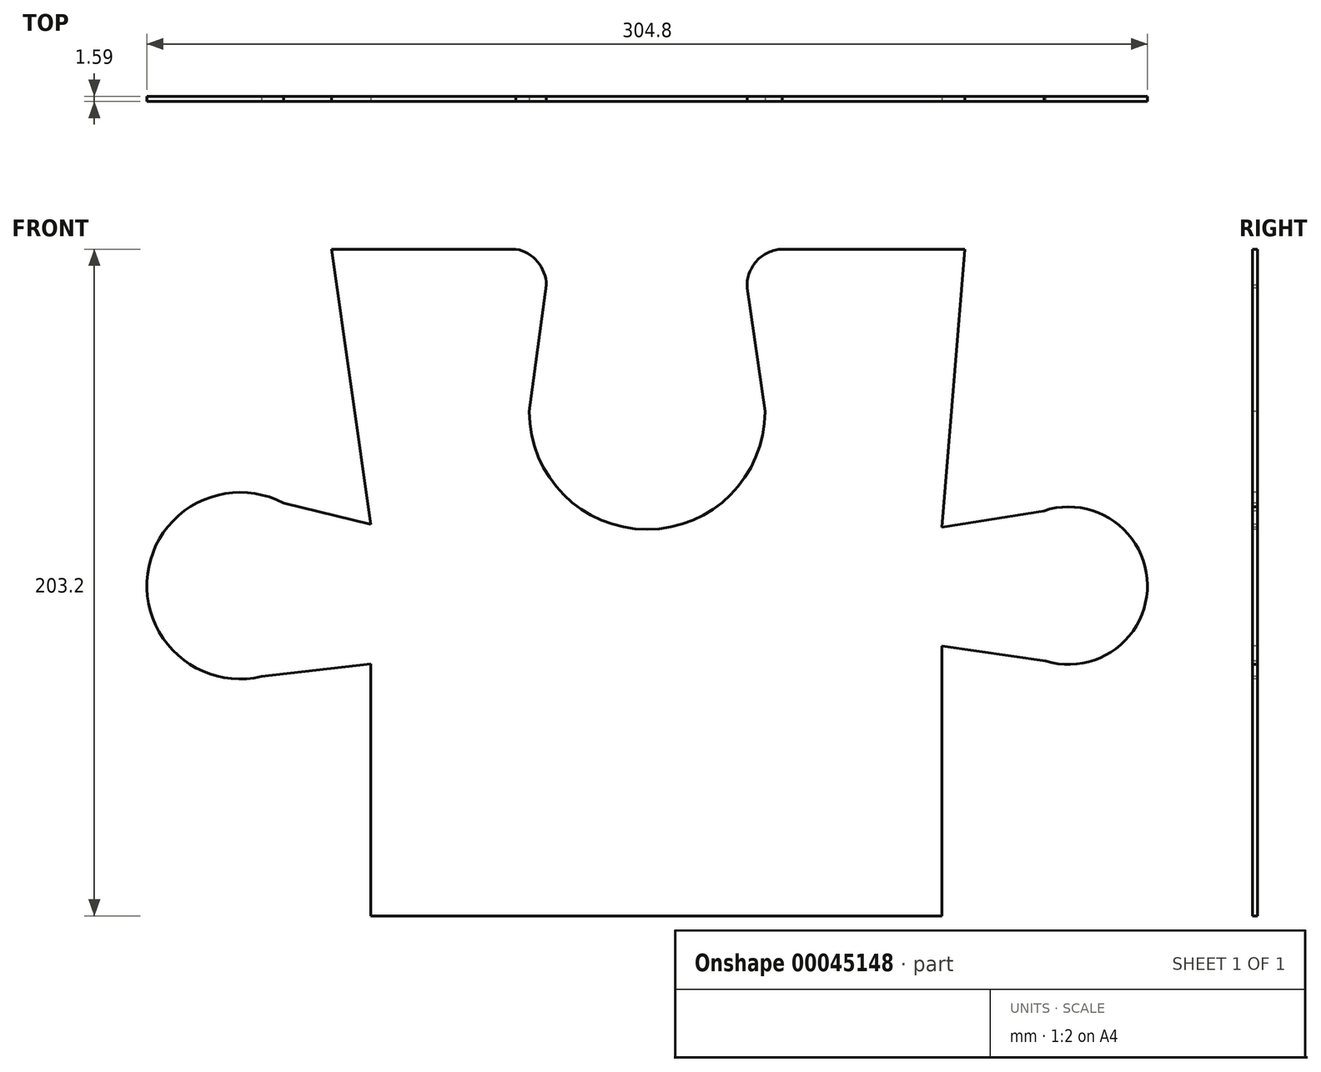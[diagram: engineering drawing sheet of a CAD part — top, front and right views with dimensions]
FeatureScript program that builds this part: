
annotation { "Feature Type Name" : "Feature", "Feature Type Description" : "" }
export const myFeature = defineFeature(function(context is Context, id is Id, definition is map)
    precondition{}
    {
        {
            var Q0;
            Q0=qCreatedBy(makeId("Front.planeOp"),FACE);
            var sketch = newSketch(context, id + "F0", { "sketchPlane" : qUnion([Q0])});
            skLineSegment(sketch, "E0.bottom", {"start": v(-101.92, -100.63) * mm, "end": v(202.88, -100.63) * mm});
            skLineSegment(sketch, "E0.top", {"start": v(-101.92, 102.57) * mm, "end": v(202.88, 102.57) * mm});
            skLineSegment(sketch, "E0.left", {"start": v(-101.92, -100.63) * mm, "end": v(-101.92, 102.57) * mm});
            skLineSegment(sketch, "E0.right", {"start": v(202.88, -100.63) * mm, "end": v(202.88, 102.57) * mm});
            skSolve(sketch);
        }
        {
            var Q0;
            Q0=makeQuery(id+"F0.imprint","IMPRINT",FACE,{"disambiguationData":[TD([[makeQuery(id+"F0.imprint","IMPRINT",EDGE,{"derivedFrom":sQuery(id+"F0.wireOp",EDGE,"E0.bottom")}),1.0]])]});
            extrude(context, id + "F1", {"entities" : qUnion([Q0]), "depth" : 1.59 * mm});
        }
        {
            var Q0;
            Q0=makeQuery(id+"F1.opExtrude","CAP_FACE",FACE,{"disambiguationData":[OSD([sQuery(id+"F0.wireOp",EDGE,"E0.bottom"),sQuery(id+"F0.wireOp",EDGE,"E0.top"),sQuery(id+"F0.wireOp",EDGE,"E0.left"),sQuery(id+"F0.wireOp",EDGE,"E0.right")])],"isStart":false});
            var sketch = newSketch(context, id + "F2", { "sketchPlane" : qUnion([Q0])});
            skCircle(sketch, "E1", {"center": v(50.48, 53.07) * mm, "radius": 35.9 * mm});
            skPoint(sketch, "E1.centerSnap0", {"position": v(50.48, 102.57) * mm});
            skLineSegment(sketch, "E2", {"start": v(14.58, 53.07) * mm, "end": v(21.26, 102.57) * mm});
            skLineSegment(sketch, "E3", {"start": v(21.26, 102.57) * mm, "end": v(79.23, 102.57) * mm});
            skLineSegment(sketch, "E4", {"start": v(79.23, 102.57) * mm, "end": v(86.38, 53.07) * mm});
            skSolve(sketch);
        }
        {
            var Q0;
            {var subQ1=sQuery(id+"F2.wireOp",EDGE,"E1");var subQ4=sQuery(id+"F2.wireOp",EDGE,"E4");var subQ5=makeQuery(id+"F2.imprint","INTERSECT",VERTEX,{"disambiguationData":[OD(1.0)],"derivedFrom":[subQ1,subQ4]});Q0=makeQuery(id+"F2.imprint","IMPRINT",FACE,{"disambiguationData":[TD([[makeQuery(id+"F2.imprint","IMPRINT",EDGE,{"disambiguationData":[TD([[subQ5,-1.0]])],"derivedFrom":subQ1}),1.0]])]});}
            var Q1;
            {var subQ4=sQuery(id+"F2.wireOp",EDGE,"E3");Q1=makeQuery(id+"F2.imprint","IMPRINT",FACE,{"disambiguationData":[TD([[makeQuery(id+"F2.imprint","IMPRINT",EDGE,{"derivedFrom":subQ4}),-1.0]])]});}
            extrude(context, id + "F3", {"entities" : qUnion([Q0, Q1]), "operationType" : NewBodyOperationType.REMOVE, "oppositeDirection" : true, "depth" : 50.8 * mm});
        }
        {
            var Q0;
            Q0=makeQuery(id+"F1.opExtrude","CAP_FACE",FACE,{"disambiguationData":[OSD([sQuery(id+"F0.wireOp",EDGE,"E0.bottom"),sQuery(id+"F0.wireOp",EDGE,"E0.top"),sQuery(id+"F0.wireOp",EDGE,"E0.left"),sQuery(id+"F0.wireOp",EDGE,"E0.right")])],"isStart":false});
            var sketch = newSketch(context, id + "F4", { "sketchPlane" : qUnion([Q0])});
            skArc(sketch, "E5", {"start": v(19.78, 91.61) * mm, "mid": v(15.62, 100.21) * mm, "end": v(6.36, 102.57) * mm});
            skSolve(sketch);
        }
        {
            var Q0;
            {var subQ1=sQuery(id+"F2.wireOp",EDGE,"E2");var subQ4=sQuery(id+"F4.wireOp",EDGE,"E5");var subQ6=makeQuery(id+"F3.boolean.opBoolean","COPY",EDGE,{"derivedFrom":makeQuery(id+"F3.opExtrude","CAP_EDGE",EDGE,{"disambiguationData":[OSD([subQ1])],"isStart":true})});var subQ8=makeQuery(id+"F4.imprint","INTERSECT",VERTEX,{"derivedFrom":[subQ6,subQ4]});Q0=makeQuery(id+"F4.imprint","IMPRINT",FACE,{"disambiguationData":[TD([[makeQuery(id+"F4.imprint","IMPRINT",EDGE,{"disambiguationData":[TD([[subQ8,-1.0]])],"derivedFrom":subQ4}),-1.0]])]});}
            extrude(context, id + "F5", {"entities" : qUnion([Q0]), "operationType" : NewBodyOperationType.REMOVE, "oppositeDirection" : true, "depth" : 50.8 * mm});
        }
        {
            var Q0;
            Q0=makeQuery(id+"F1.opExtrude","CAP_FACE",FACE,{"disambiguationData":[OSD([sQuery(id+"F0.wireOp",EDGE,"E0.bottom"),sQuery(id+"F0.wireOp",EDGE,"E0.top"),sQuery(id+"F0.wireOp",EDGE,"E0.left"),sQuery(id+"F0.wireOp",EDGE,"E0.right")])],"isStart":false});
            var sketch = newSketch(context, id + "F6", { "sketchPlane" : qUnion([Q0])});
            skArc(sketch, "E6", {"start": v(92.48, 102.57) * mm, "mid": v(84.07, 99.2) * mm, "end": v(80.94, 90.7) * mm});
            skSolve(sketch);
        }
        {
            var Q0;
            Q0 = qSketchRegion(id + "F6", true);
            var Q1;
            {var subQ1=sQuery(id+"F2.wireOp",EDGE,"E4");var subQ4=sQuery(id+"F6.wireOp",EDGE,"E6");var subQ6=makeQuery(id+"F3.boolean.opBoolean","COPY",EDGE,{"derivedFrom":makeQuery(id+"F3.opExtrude","CAP_EDGE",EDGE,{"disambiguationData":[OSD([subQ1])],"isStart":true})});var subQ8=makeQuery(id+"F6.imprint","INTERSECT",VERTEX,{"derivedFrom":[subQ6,subQ4]});Q1=makeQuery(id+"F6.imprint","IMPRINT",FACE,{"disambiguationData":[TD([[makeQuery(id+"F6.imprint","IMPRINT",EDGE,{"disambiguationData":[TD([[subQ8,1.0]])],"derivedFrom":subQ4}),-1.0]])]});}
            extrude(context, id + "F7", {"entities" : qUnion([Q0, Q1]), "operationType" : NewBodyOperationType.REMOVE, "oppositeDirection" : true, "depth" : 50.8 * mm});
        }
        {
            var Q0;
            Q0=makeQuery(id+"F1.opExtrude","CAP_FACE",FACE,{"disambiguationData":[OSD([sQuery(id+"F0.wireOp",EDGE,"E0.bottom"),sQuery(id+"F0.wireOp",EDGE,"E0.top"),sQuery(id+"F0.wireOp",EDGE,"E0.left"),sQuery(id+"F0.wireOp",EDGE,"E0.right")])],"isStart":false});
            var sketch = newSketch(context, id + "F8", { "sketchPlane" : qUnion([Q0])});
            skLineSegment(sketch, "E7", {"start": v(-45.7, 102.57) * mm, "end": v(-33.74, 18.68) * mm});
            skCircle(sketch, "E8", {"center": v(-73.49, 0) * mm, "radius": 28.44 * mm});
            skLineSegment(sketch, "E9", {"start": v(-73.49, 28.44) * mm, "end": v(-33.74, 18.68) * mm});
            skLineSegment(sketch, "E10", {"start": v(-33.74, 18.68) * mm, "end": v(-33.74, -100.63) * mm});
            skLineSegment(sketch, "E11", {"start": v(-73.49, -28.44) * mm, "end": v(-33.74, -23.83) * mm});
            skSolve(sketch);
        }
        {
            var Q0;
            {var subQ7=sQuery(id+"F8.wireOp",EDGE,"E7");Q0=makeQuery(id+"F8.imprint","IMPRINT",FACE,{"disambiguationData":[TD([[makeQuery(id+"F8.imprint","IMPRINT",EDGE,{"derivedFrom":subQ7}),-1.0]])]});}
            extrude(context, id + "F9", {"entities" : qUnion([Q0]), "operationType" : NewBodyOperationType.REMOVE, "oppositeDirection" : true, "depth" : 50.8 * mm});
        }
        {
            var Q0;
            {var subQ1=sQuery(id+"F8.wireOp",EDGE,"E8");var subQ7=sQuery(id+"F8.wireOp",EDGE,"E11");var subQ8=makeQuery(id+"F8.imprint","INTERSECT",VERTEX,{"disambiguationData":[OD(0.0)],"derivedFrom":[subQ1,subQ7]});Q0=makeQuery(id+"F8.imprint","IMPRINT",FACE,{"disambiguationData":[TD([[makeQuery(id+"F8.imprint","IMPRINT",EDGE,{"disambiguationData":[TD([[subQ8,1.0]])],"derivedFrom":subQ1}),-1.0]])]});}
            extrude(context, id + "F10", {"entities" : qUnion([Q0]), "operationType" : NewBodyOperationType.REMOVE, "oppositeDirection" : true, "depth" : 50.8 * mm});
        }
        {
            var Q0;
            Q0=makeQuery(id+"F1.opExtrude","CAP_FACE",FACE,{"disambiguationData":[OSD([sQuery(id+"F0.wireOp",EDGE,"E0.bottom"),sQuery(id+"F0.wireOp",EDGE,"E0.top"),sQuery(id+"F0.wireOp",EDGE,"E0.left"),sQuery(id+"F0.wireOp",EDGE,"E0.right")])],"isStart":false});
            var sketch = newSketch(context, id + "F11", { "sketchPlane" : qUnion([Q0])});
            skLineSegment(sketch, "E12", {"start": v(147.25, 102.57) * mm, "end": v(140.32, 17.84) * mm});
            skCircle(sketch, "E13", {"center": v(178.85, 0) * mm, "radius": 24.02 * mm});
            skLineSegment(sketch, "E14", {"start": v(178.85, 24.02) * mm, "end": v(140.32, 17.84) * mm});
            skLineSegment(sketch, "E15", {"start": v(178.85, -24.02) * mm, "end": v(140.32, -18.37) * mm});
            skLineSegment(sketch, "E16", {"start": v(140.32, -18.37) * mm, "end": v(140.32, 17.84) * mm});
            skLineSegment(sketch, "E17", {"start": v(140.32, -18.37) * mm, "end": v(140.32, -100.63) * mm});
            skSolve(sketch);
        }
        {
            var Q0;
            {var subQ7=sQuery(id+"F11.wireOp",EDGE,"E12");Q0=makeQuery(id+"F11.imprint","IMPRINT",FACE,{"disambiguationData":[TD([[makeQuery(id+"F11.imprint","IMPRINT",EDGE,{"derivedFrom":subQ7}),1.0]])]});}
            extrude(context, id + "F12", {"entities" : qUnion([Q0]), "operationType" : NewBodyOperationType.REMOVE, "oppositeDirection" : true, "depth" : 50.8 * mm});
        }
        {
            var Q0;
            {var subQ1=sQuery(id+"F11.wireOp",EDGE,"E17");Q0=makeQuery(id+"F11.imprint","IMPRINT",FACE,{"disambiguationData":[TD([[makeQuery(id+"F11.imprint","IMPRINT",EDGE,{"derivedFrom":subQ1}),1.0]])]});}
            extrude(context, id + "F13", {"entities" : qUnion([Q0]), "operationType" : NewBodyOperationType.REMOVE, "oppositeDirection" : true, "depth" : 50.8 * mm});
        }
    });
